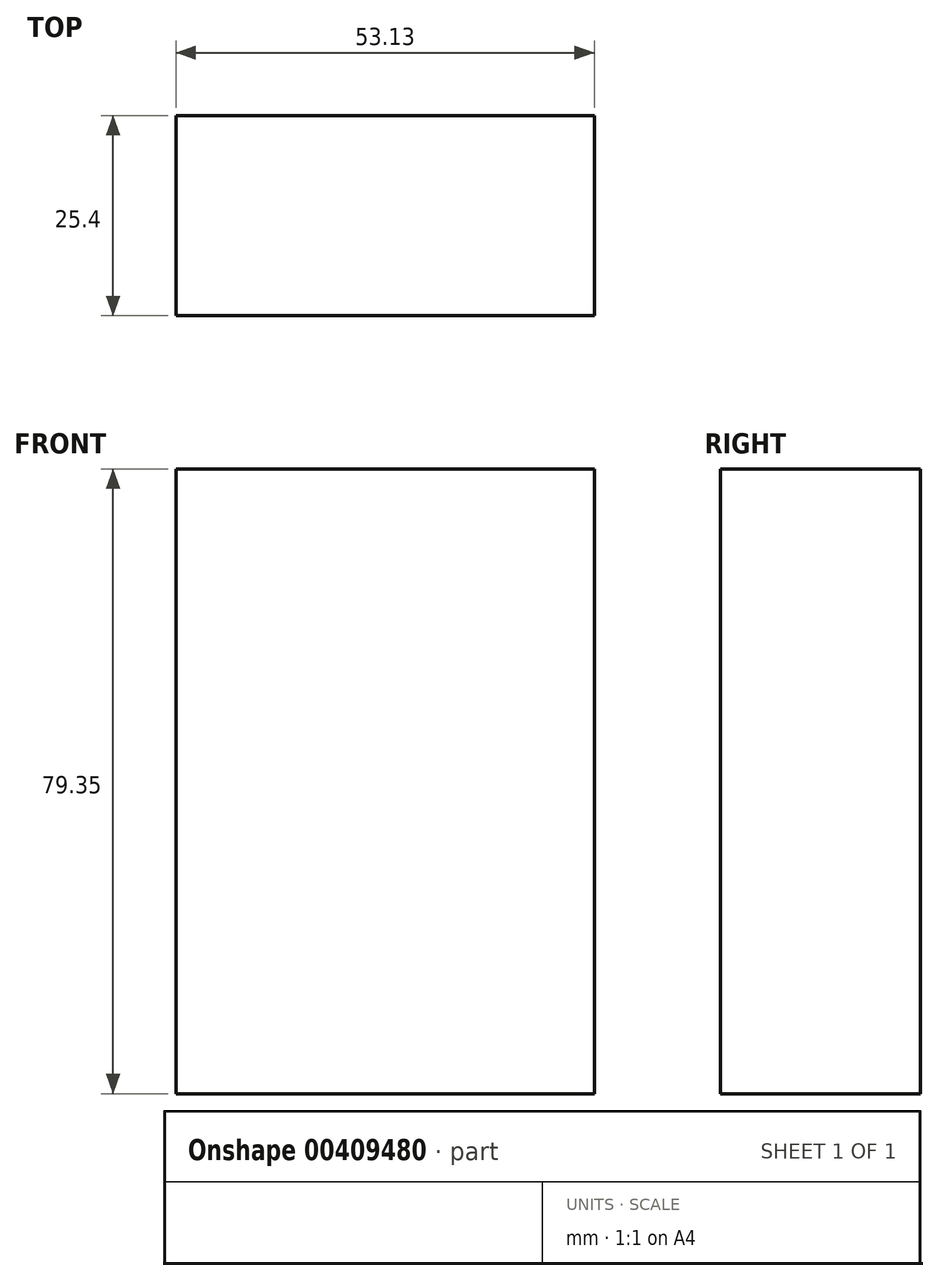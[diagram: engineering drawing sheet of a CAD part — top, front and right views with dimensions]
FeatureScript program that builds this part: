
annotation { "Feature Type Name" : "Feature", "Feature Type Description" : "" }
export const myFeature = defineFeature(function(context is Context, id is Id, definition is map)
    precondition{}
    {
        {
            var Q0;
            Q0=qCreatedBy(makeId("Front.planeOp"),FACE);
            var sketch = newSketch(context, id + "F0", { "sketchPlane" : qUnion([Q0])});
            skLineSegment(sketch, "E0.bottom", {"start": v(0, 32.81) * mm, "end": v(53.13, 32.81) * mm});
            skLineSegment(sketch, "E0.top", {"start": v(0, -46.54) * mm, "end": v(53.13, -46.54) * mm});
            skLineSegment(sketch, "E0.left", {"start": v(0, 32.81) * mm, "end": v(0, -46.54) * mm});
            skLineSegment(sketch, "E0.right", {"start": v(53.13, 32.81) * mm, "end": v(53.13, -46.54) * mm});
            skSolve(sketch);
        }
        {
            var Q0;
            Q0=makeQuery(id+"F0.imprint","IMPRINT",FACE,{"disambiguationData":[TD([[makeQuery(id+"F0.imprint","IMPRINT",EDGE,{"derivedFrom":sQuery(id+"F0.wireOp",EDGE,"E0.bottom")}),-1.0]])]});
            extrude(context, id + "F1", {"entities" : qUnion([Q0]), "depth" : 25.4 * mm});
        }
    });
